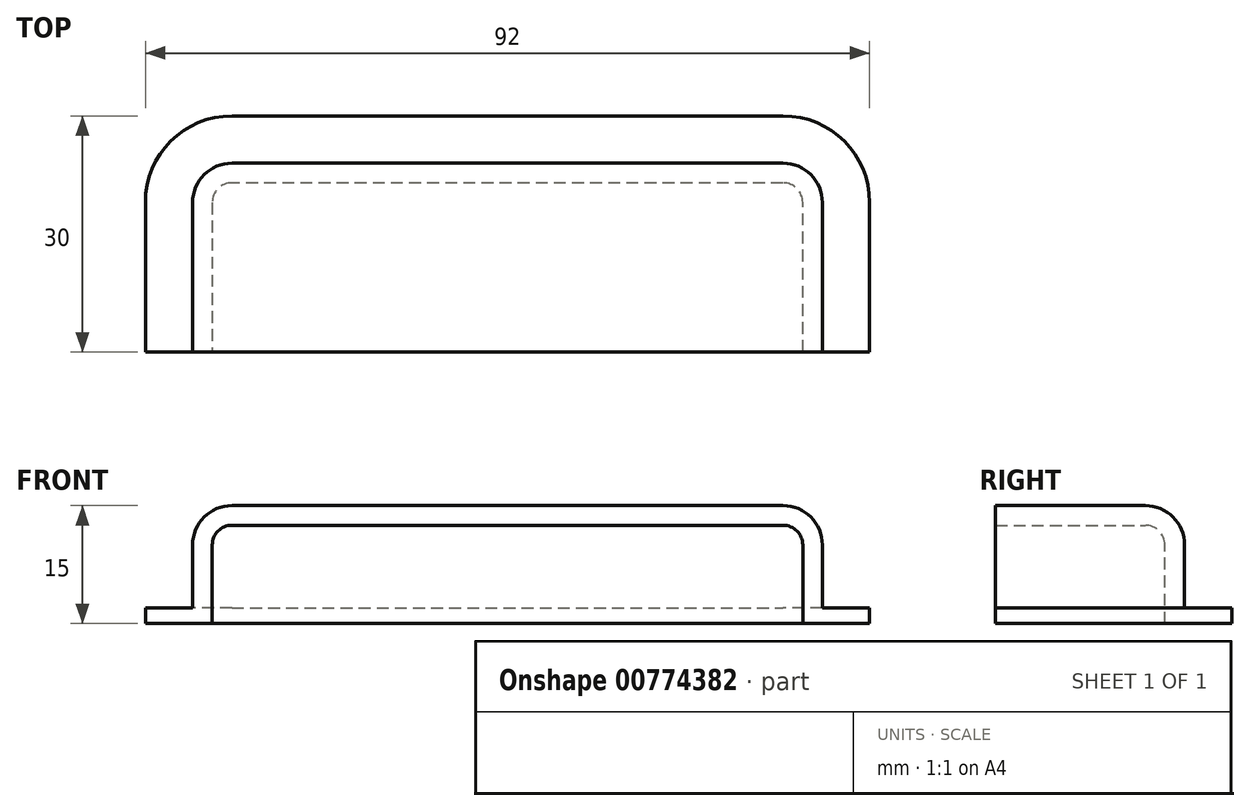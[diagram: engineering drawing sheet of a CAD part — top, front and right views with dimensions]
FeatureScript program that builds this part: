
annotation { "Feature Type Name" : "Feature", "Feature Type Description" : "" }
export const myFeature = defineFeature(function(context is Context, id is Id, definition is map)
    precondition{}
    {
        {
            var Q0;
            Q0=qCreatedBy(makeId("Top.planeOp"),FACE);
            var sketch = newSketch(context, id + "F0", { "sketchPlane" : qUnion([Q0])});
            skLineSegment(sketch, "E0.bottom", {"start": v(-46, 0) * mm, "end": v(-40, 0) * mm});
            skLineSegment(sketch, "E0.top", {"start": v(-35, 30) * mm, "end": v(35, 30) * mm});
            skLineSegment(sketch, "E0.left", {"start": v(-46, 0) * mm, "end": v(-46, 19) * mm});
            skLineSegment(sketch, "E0.right", {"start": v(46, 0) * mm, "end": v(46, 19) * mm});
            skLineSegment(sketch, "E1.top", {"start": v(-35, 24) * mm, "end": v(35, 24) * mm});
            skLineSegment(sketch, "E1.left", {"start": v(-40, 0) * mm, "end": v(-40, 19) * mm});
            skLineSegment(sketch, "E1.right", {"start": v(40, 0) * mm, "end": v(40, 19) * mm});
            skLineSegment(sketch, "E2.trimOffspring", {"start": v(40, 0) * mm, "end": v(46, 0) * mm});
            skPoint(sketch, "E3.visualSharp", {"position": v(40, 24) * mm});
            skArc(sketch, "E3.filletArc", {"start": v(40, 19) * mm, "mid": v(38.54, 22.54) * mm, "end": v(35, 24) * mm});
            skPoint(sketch, "E4.visualSharp", {"position": v(46, 30) * mm});
            skArc(sketch, "E4.filletArc", {"start": v(46, 19) * mm, "mid": v(42.78, 26.78) * mm, "end": v(35, 30) * mm});
            skPoint(sketch, "E5.visualSharp", {"position": v(-40, 24) * mm});
            skArc(sketch, "E5.filletArc", {"start": v(-35, 24) * mm, "mid": v(-38.54, 22.54) * mm, "end": v(-40, 19) * mm});
            skPoint(sketch, "E6.visualSharp", {"position": v(-46, 30) * mm});
            skArc(sketch, "E6.filletArc", {"start": v(-35, 30) * mm, "mid": v(-42.78, 26.78) * mm, "end": v(-46, 19) * mm});
            skSolve(sketch);
        }
        {
            var Q0;
            Q0 = qSketchRegion(id + "F0", true);
            extrude(context, id + "F1", {"entities" : qUnion([Q0]), "depth" : 2 * mm, "offsetDistance" : 25 * mm});
        }
        {
            var Q0;
            Q0=qCreatedBy(makeId("Top.planeOp"),FACE);
            var sketch = newSketch(context, id + "F2", { "sketchPlane" : qUnion([Q0])});
            skLineSegment(sketch, "E7.0", {"start": v(40, 0) * mm, "end": v(40, 19) * mm});
            skLineSegment(sketch, "E7.1", {"start": v(-40, 0) * mm, "end": v(-40, 19) * mm});
            skArc(sketch, "E7.2", {"start": v(-35, 24) * mm, "mid": v(-38.54, 22.54) * mm, "end": v(-40, 19) * mm});
            skLineSegment(sketch, "E7.3", {"start": v(-35, 24) * mm, "end": v(35, 24) * mm});
            skArc(sketch, "E7.4", {"start": v(40, 19) * mm, "mid": v(38.54, 22.54) * mm, "end": v(35, 24) * mm});
            skLineSegment(sketch, "E8", {"start": v(-40, 0) * mm, "end": v(40, 0) * mm});
            skSolve(sketch);
        }
        {
            var Q0;
            Q0 = qSketchRegion(id + "F2", true);
            extrude(context, id + "F3", {"entities" : qUnion([Q0]), "operationType" : NewBodyOperationType.ADD, "depth" : 15 * mm, "offsetDistance" : 25 * mm});
        }
        {
            var Q0;
            Q0=makeQuery(id+"F3.opExtrude","CAP_EDGE",EDGE,{"disambiguationData":[OSD([sQuery(id+"F2.wireOp",EDGE,"E7.1")])],"isStart":false});
            fillet(context, id + "F4", {"entities" : qUnion([Q0]), "radius" : 5 * mm, "tangentPropagation" : true, "allowEdgeOverflow" : false});
        }
        {
            var Q0;
            Q0=makeQuery(id+"F3.boolean.opBoolean","MERGE",FACE,{"derivedFrom":[makeQuery(id+"F1.opExtrude","SWEPT_FACE",FACE,{"disambiguationData":[OSD([sQuery(id+"F0.wireOp",EDGE,"E0.bottom")])]}),makeQuery(id+"F1.opExtrude","SWEPT_FACE",FACE,{"disambiguationData":[OSD([sQuery(id+"F0.wireOp",EDGE,"E2.trimOffspring")])]}),makeQuery(id+"F3.opExtrude","SWEPT_FACE",FACE,{"disambiguationData":[OSD([sQuery(id+"F2.wireOp",EDGE,"E8")])]})]});
            shell(context, id + "F5", {"entities" : qUnion([Q0]), "thickness" : 2.5 * mm});
        }
        {
            var Q0;
            Q0=makeQuery(id+"F5.opShell","OFFSET_FACE",FACE,{"disambiguationData":[OSD([sQuery(id+"F0.wireOp",EDGE,"E0.bottom"),sQuery(id+"F0.wireOp",EDGE,"E0.top"),sQuery(id+"F0.wireOp",EDGE,"E0.left"),sQuery(id+"F0.wireOp",EDGE,"E0.right"),sQuery(id+"F0.wireOp",EDGE,"E1.top"),sQuery(id+"F0.wireOp",EDGE,"E1.left"),sQuery(id+"F0.wireOp",EDGE,"E1.right"),sQuery(id+"F0.wireOp",EDGE,"E2.trimOffspring"),sQuery(id+"F0.wireOp",EDGE,"E3.filletArc"),sQuery(id+"F0.wireOp",EDGE,"E4.filletArc"),sQuery(id+"F0.wireOp",EDGE,"E5.filletArc"),sQuery(id+"F0.wireOp",EDGE,"E6.filletArc"),sQuery(id+"F2.wireOp",EDGE,"E7.0"),sQuery(id+"F2.wireOp",EDGE,"E7.1"),sQuery(id+"F2.wireOp",EDGE,"E7.2"),sQuery(id+"F2.wireOp",EDGE,"E7.3"),sQuery(id+"F2.wireOp",EDGE,"E7.4"),sQuery(id+"F2.wireOp",EDGE,"E8")])]});
            var sketch = newSketch(context, id + "F6", { "sketchPlane" : qUnion([Q0])});
            skArc(sketch, "E9.0", {"start": v(35, 21.5) * mm, "mid": v(36.77, 20.77) * mm, "end": v(37.5, 19) * mm});
            skArc(sketch, "E9.1", {"start": v(-37.5, 19) * mm, "mid": v(-36.77, 20.77) * mm, "end": v(-35, 21.5) * mm});
            skLineSegment(sketch, "E9.2", {"start": v(-37.5, 19) * mm, "end": v(-37.5, 0) * mm});
            skLineSegment(sketch, "E9.3", {"start": v(35, 21.5) * mm, "end": v(-35, 21.5) * mm});
            skLineSegment(sketch, "E9.4", {"start": v(-37.5, 0) * mm, "end": v(37.5, 0) * mm});
            skLineSegment(sketch, "E9.5", {"start": v(37.5, 0) * mm, "end": v(37.5, 19) * mm});
            skSolve(sketch);
        }
        {
            var Q0;
            Q0 = qSketchRegion(id + "F6", true);
            extrude(context, id + "F7", {"entities" : qUnion([Q0]), "operationType" : NewBodyOperationType.REMOVE, "oppositeDirection" : true, "depth" : 25 * mm, "offsetDistance" : 25 * mm});
        }
    });
